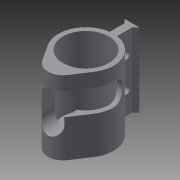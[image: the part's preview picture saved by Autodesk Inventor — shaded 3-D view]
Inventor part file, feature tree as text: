
AUTODESK INVENTOR PART (.ipt)
format: ipt  version: 2015 (Build 190159000, 159)  size: 168,448 bytes
history: native  units: in
note: dims shown in document units (in); Inventor stores cm internally (conversion verified against a paired STEP export)
features: extrude x6, sketch x6
ambient origin geometry x8: Origin, YZ Plane, XZ Plane, XY Plane, X Axis, Y Axis, Z Axis, Center Point
bodies: Solid1 (feature_tree)
feature tree (12):
  extrude  "Extrusion1"  Depth=2.0in
  extrude  "Extrusion2"  Depth=0.5in
  extrude  "Extrusion3"  Depth=0.61in TaperAngle=0.0deg
  extrude  "Extrusion4"  Depth=0.5in
  extrude  "Extrusion5"  Depth=2.0in TaperAngle=0.0deg
  extrude  "Extrusion6"  Depth=0.18in
  sketch  "Sketch1"  dims[d0=1.5in d1=2.0in d2=0.0in d3=1.25in]
  sketch  "Sketch2"  dims[d4=1.875in d5=0.0in d6=0.5in]
  sketch  "Sketch3"  dims[d7=0.61in d8=1.75in d9=0.0in]
  sketch  "Sketch4"  dims[d11=1.75in d12=0.0in d13=0.5in]
  sketch  "Sketch5"  dims[d14=0.2in d17=2.0in d18=0.0in]
  sketch  "Sketch6"  dims[d19=0.18in d20=0.18in d23=0.5in d24=0.5in d25=1.75in d26=0.0in d27=0.4in]
